annotation { "Feature Type Name" : "Feature", "Feature Type Description" : "" }
export const myFeature = defineFeature(function(context is Context, id is Id, definition is map)
    precondition{}
    {
        {
            var Q0;
            Q0=qCreatedBy(makeId("Front.planeOp"),FACE);
            var sketch = newSketch(context, id + "F0", { "sketchPlane" : qUnion([Q0])});
            skCircle(sketch, "E0.cCircle", {"center": v(0, 0) * mm, "radius": 5.2 * mm, "construction": true});
            skLineSegment(sketch, "E0.0", {"start": v(-3, 5.2) * mm, "end": v(3, 5.2) * mm});
            skLineSegment(sketch, "E0.1", {"start": v(3, 5.2) * mm, "end": v(6.01, 0) * mm});
            skLineSegment(sketch, "E0.2", {"start": v(6.01, 0) * mm, "end": v(3, -5.2) * mm});
            skLineSegment(sketch, "E0.3", {"start": v(3, -5.2) * mm, "end": v(-3, -5.2) * mm});
            skLineSegment(sketch, "E0.4", {"start": v(-3, -5.2) * mm, "end": v(-6.01, 0) * mm});
            skLineSegment(sketch, "E0.5", {"start": v(-6.01, 0) * mm, "end": v(-3, 5.2) * mm});
            skPoint(sketch, "E0.0.midPoint", {"position": v(0, 5.2) * mm});
            skSolve(sketch);
        }
        {
            var Q0;
            Q0=makeQuery(id+"F0.imprint","IMPRINT",FACE,{"disambiguationData":[TD([[makeQuery(id+"F0.imprint","IMPRINT",EDGE,{"derivedFrom":sQuery(id+"F0.wireOp",EDGE,"E0.0")}),-1.0]])]});
            extrude(context, id + "F1", {"entities" : qUnion([Q0]), "depth" : 50.8 * mm, "offsetDistance" : 25.4 * mm});
        }
        {
            var Q0;
            Q0=makeQuery(id+"F1.opExtrude","CAP_FACE",FACE,{"disambiguationData":[OSD([sQuery(id+"F0.wireOp",EDGE,"E0.0"),sQuery(id+"F0.wireOp",EDGE,"E0.1"),sQuery(id+"F0.wireOp",EDGE,"E0.2"),sQuery(id+"F0.wireOp",EDGE,"E0.3"),sQuery(id+"F0.wireOp",EDGE,"E0.4"),sQuery(id+"F0.wireOp",EDGE,"E0.5")])],"isStart":false});
            var sketch = newSketch(context, id + "F2", { "sketchPlane" : qUnion([Q0])});
            skCircle(sketch, "E1.cCircle", {"center": v(0, 0) * mm, "radius": 3.62 * mm, "construction": true});
            skLineSegment(sketch, "E1.0", {"start": v(-2.09, 3.62) * mm, "end": v(2.09, 3.62) * mm});
            skLineSegment(sketch, "E1.1", {"start": v(2.09, 3.62) * mm, "end": v(4.18, 0) * mm});
            skLineSegment(sketch, "E1.2", {"start": v(4.18, 0) * mm, "end": v(2.09, -3.62) * mm});
            skLineSegment(sketch, "E1.3", {"start": v(2.09, -3.62) * mm, "end": v(-2.09, -3.62) * mm});
            skLineSegment(sketch, "E1.4", {"start": v(-2.09, -3.62) * mm, "end": v(-4.18, 0) * mm});
            skLineSegment(sketch, "E1.5", {"start": v(-4.18, 0) * mm, "end": v(-2.09, 3.62) * mm});
            skPoint(sketch, "E1.0.midPoint", {"position": v(0, 3.62) * mm});
            skSolve(sketch);
        }
        {
            var Q0;
            Q0=makeQuery(id+"F2.imprint","IMPRINT",FACE,{"disambiguationData":[TD([[makeQuery(id+"F2.imprint","IMPRINT",EDGE,{"derivedFrom":sQuery(id+"F2.wireOp",EDGE,"E1.0")}),-1.0]])]});
            extrude(context, id + "F3", {"entities" : qUnion([Q0]), "operationType" : NewBodyOperationType.REMOVE, "oppositeDirection" : true, "depth" : 25.4 * mm, "offsetDistance" : 25.4 * mm});
        }
        {
            var Q0;
            Q0=makeQuery(id+"F1.opExtrude","CAP_FACE",FACE,{"disambiguationData":[OSD([sQuery(id+"F0.wireOp",EDGE,"E0.0"),sQuery(id+"F0.wireOp",EDGE,"E0.1"),sQuery(id+"F0.wireOp",EDGE,"E0.2"),sQuery(id+"F0.wireOp",EDGE,"E0.3"),sQuery(id+"F0.wireOp",EDGE,"E0.4"),sQuery(id+"F0.wireOp",EDGE,"E0.5")])],"isStart":true});
            var sketch = newSketch(context, id + "F4", { "sketchPlane" : qUnion([Q0])});
            skCircle(sketch, "E2", {"center": v(0, 0) * mm, "radius": 3.94 * mm});
            skSolve(sketch);
        }
        {
            var Q0;
            Q0=makeQuery(id+"F4.imprint","IMPRINT",FACE,{"disambiguationData":[TD([[makeQuery(id+"F4.imprint","IMPRINT",EDGE,{"derivedFrom":sQuery(id+"F4.wireOp",EDGE,"E2")}),1.0]])]});
            extrude(context, id + "F5", {"entities" : qUnion([Q0]), "operationType" : NewBodyOperationType.REMOVE, "oppositeDirection" : true, "depth" : 25.4 * mm, "offsetDistance" : 25.4 * mm});
        }
        {
            var Q0;
            Q0=makeQuery(id+"F1.opExtrude","SWEPT_FACE",FACE,{"disambiguationData":[OSD([sQuery(id+"F0.wireOp",EDGE,"E0.0")])]});
            var sketch = newSketch(context, id + "F6", { "sketchPlane" : qUnion([Q0])});
            skLineSegment(sketch, "E3", {"start": v(0, -5.63) * mm, "end": v(-2.29, -9.14) * mm});
            skLineSegment(sketch, "E4", {"start": v(-2.29, -9.14) * mm, "end": v(-1.27, -9.14) * mm});
            skLineSegment(sketch, "E5", {"start": v(-1.27, -9.14) * mm, "end": v(-1.27, -21.77) * mm});
            skLineSegment(sketch, "E6", {"start": v(-1.27, -21.77) * mm, "end": v(1.27, -21.77) * mm});
            skLineSegment(sketch, "E7", {"start": v(1.27, -21.77) * mm, "end": v(1.27, -9.14) * mm});
            skLineSegment(sketch, "E8", {"start": v(1.27, -9.14) * mm, "end": v(2.29, -9.14) * mm});
            skLineSegment(sketch, "E9", {"start": v(2.29, -9.14) * mm, "end": v(0, -5.63) * mm});
            skSolve(sketch);
        }
        {
            var Q0;
            Q0=makeQuery(id+"F6.imprint","IMPRINT",FACE,{"disambiguationData":[TD([[makeQuery(id+"F6.imprint","IMPRINT",EDGE,{"derivedFrom":sQuery(id+"F6.wireOp",EDGE,"E3")}),1.0]])]});
            extrude(context, id + "F7", {"entities" : qUnion([Q0]), "operationType" : NewBodyOperationType.REMOVE, "oppositeDirection" : true, "depth" : 0.5 * mm, "offsetDistance" : 25.4 * mm});
        }
        {
            var Q0;
            Q0=makeQuery(id+"F1.opExtrude","SWEPT_FACE",FACE,{"disambiguationData":[OSD([sQuery(id+"F0.wireOp",EDGE,"E0.3")])]});
            var sketch = newSketch(context, id + "F8", { "sketchPlane" : qUnion([Q0])});
            skText(sketch, "E10", { "text": "CHRIS JENTZSCH", "fontName": "OpenSans-Regular.ttf"});
            const initialGuessF8  = {"E10": [-0.00094, 0.03796, 0, -1, 0.00239]};
            skSetInitialGuess(sketch, initialGuessF8);
            skSolve(sketch);
        }
        {
            var Q0;
            Q0 = qSketchRegion(id + "F8", true);
            extrude(context, id + "F9", {"entities" : qUnion([Q0]), "operationType" : NewBodyOperationType.REMOVE, "oppositeDirection" : true, "depth" : 0.5 * mm, "offsetDistance" : 25.4 * mm});
        }
    });